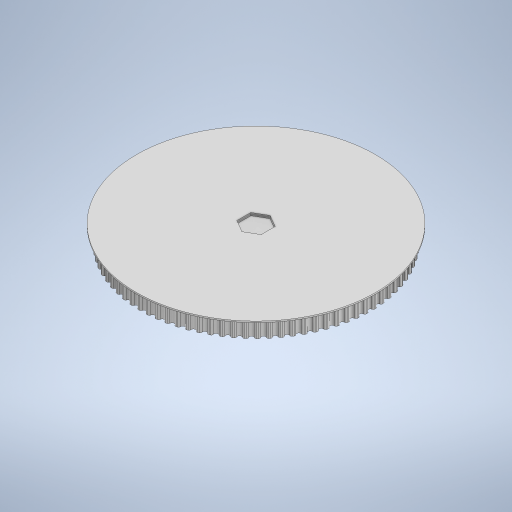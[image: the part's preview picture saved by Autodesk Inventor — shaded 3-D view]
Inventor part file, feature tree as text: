
AUTODESK INVENTOR PART (.ipt)
format: ipt  version: 2024 (Build 280153000, 153)  size: 1,247,232 bytes
history: native  units: mm
features: sketch x7, extrude x6, pattern_circular x1, fillet x1, chamfer x1, projected_geometry x1
ambient origin geometry x8: Origin, YZ Plane, XZ Plane, XY Plane, X Axis, Y Axis, Z Axis, Center Point
bodies: Solid1 (feature_tree)
feature tree (17):
  extrude  "Extrusion1"  Depth=25.0mm TaperAngle=0.0deg
  extrude  "Extrusion2"  Depth=2.0mm TaperAngle=0.0deg
  extrude  "Extrusion3"  Depth=164.0mm
  extrude  "Extrusion4"  Depth=10.0mm TaperAngle=360.0deg
  pattern_circular  "Circular Pattern1"  [2 undecoded]
  extrude  "Extrusion5"  Depth=1.15mm
  extrude  "Extrusion6"  Depth=4.0mm TaperAngle=45.0deg
  fillet  "Fillet1"  [1 undecoded]
  sketch  "Sketch8"  dims[d18=3.0mm d19=3.0mm d20=0.0mm d21=1.15mm d23=4.0mm d24=2.0mm d25=45.0deg]
  chamfer  "Chamfer1"  [1 undecoded]
  sketch  "Sketch1"  dims[d0=20.0mm d1=25.0mm d2=0.0mm]
  sketch  "Sketch2"  dims[d3=40.0mm d4=2.0mm d5=0.0mm]
  sketch  "Sketch3"  dims[d6=13.0mm d7=0.0mm d8=164.0mm]
  sketch  "Sketch4"  dims[d9=10.0mm d10=0.0mm d11=850.0mm d12=360.0deg]
  sketch  "Sketch6"  dims[d15=2.0mm d16=0.0mm]
  sketch  "Sketch7"  dims[d17=10.0mm]
  projected_geometry  "Projected Loop1"
note: 4 required parameter values undecoded (feature->parameter linkage not recoverable at this tier; creation-order binding heuristic only, values carry confidence <= 0.55)
